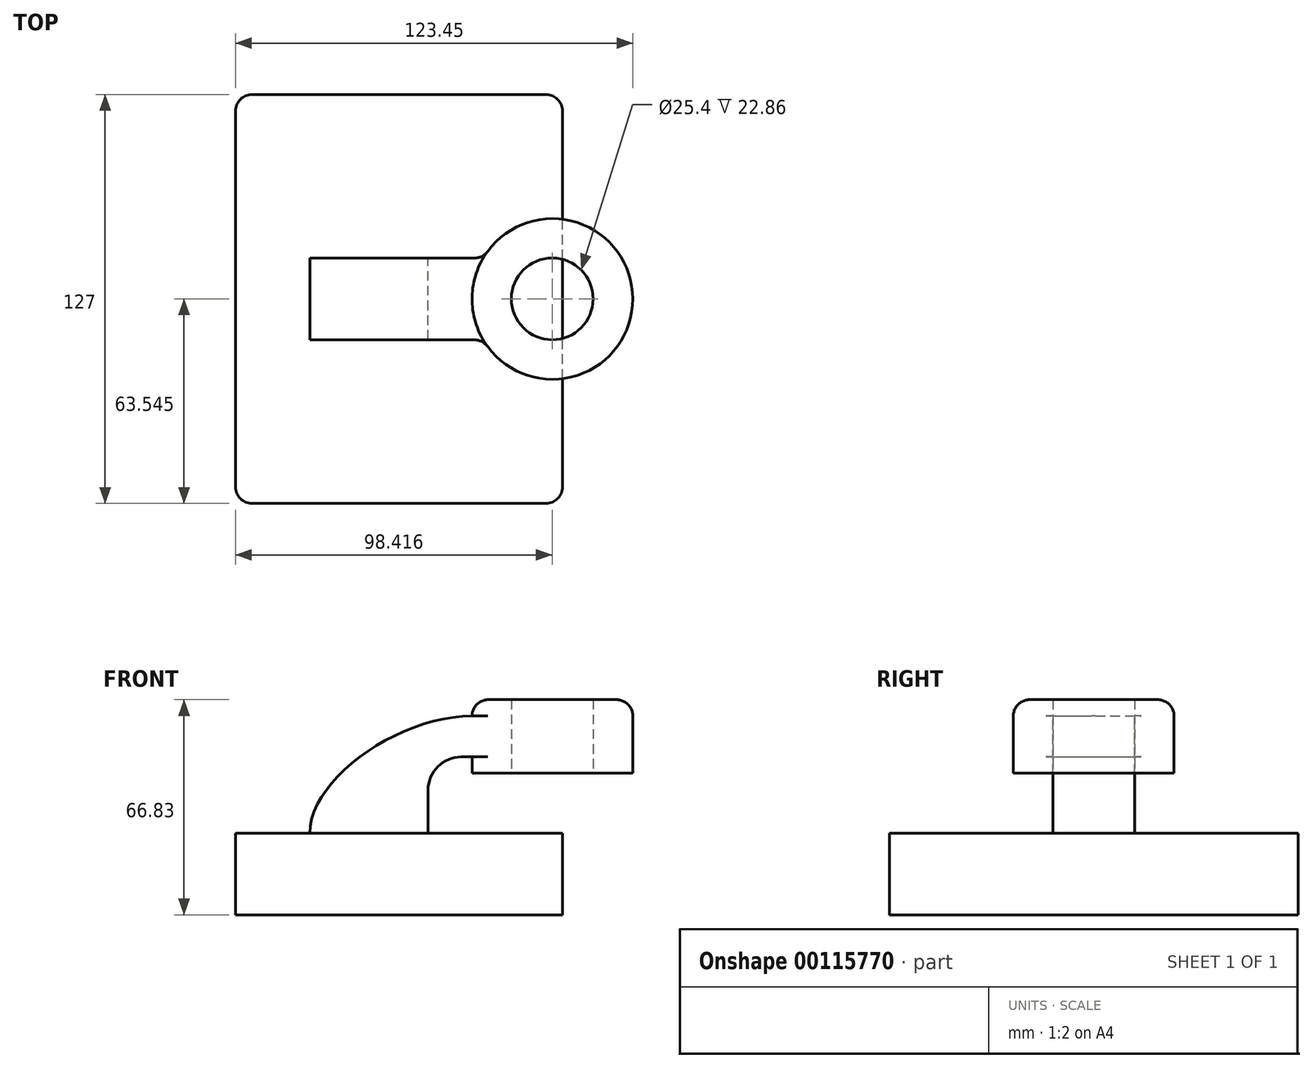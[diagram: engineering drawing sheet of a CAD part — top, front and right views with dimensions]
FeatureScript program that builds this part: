
annotation { "Feature Type Name" : "Feature", "Feature Type Description" : "" }
export const myFeature = defineFeature(function(context is Context, id is Id, definition is map)
    precondition{}
    {
        {
            var Q0;
            Q0=qCreatedBy(makeId("Front.planeOp"),FACE);
            var sketch = newSketch(context, id + "F0", { "sketchPlane" : qUnion([Q0])});
            skLineSegment(sketch, "E0.bottom", {"start": v(-50.8, 12.7) * mm, "end": v(50.8, 12.7) * mm});
            skLineSegment(sketch, "E0.top", {"start": v(-50.8, -12.7) * mm, "end": v(50.8, -12.7) * mm});
            skLineSegment(sketch, "E0.left", {"start": v(-50.8, 12.7) * mm, "end": v(-50.8, -12.7) * mm});
            skLineSegment(sketch, "E0.right", {"start": v(50.8, 12.7) * mm, "end": v(50.8, -12.7) * mm});
            skPoint(sketch, "E0.middle", {"position": v(0, 0) * mm});
            skPoint(sketch, "E1.visualSharp", {"position": v(35.5, 28.49) * mm});
            skLineSegment(sketch, "E2.bottom", {"start": v(22.69, 54.13) * mm, "end": v(72.65, 54.13) * mm});
            skLineSegment(sketch, "E2.top", {"start": v(22.69, 31.27) * mm, "end": v(72.65, 31.27) * mm});
            skLineSegment(sketch, "E2.left", {"start": v(22.69, 54.13) * mm, "end": v(22.69, 31.27) * mm});
            skLineSegment(sketch, "E2.right", {"start": v(72.65, 54.13) * mm, "end": v(72.65, 31.27) * mm});
            skLineSegment(sketch, "E3", {"start": v(47.67, 54.13) * mm, "end": v(47.67, 31.27) * mm});
            skLineSegment(sketch, "E4.0", {"start": v(47.67, 49.05) * mm, "end": v(22.7, 49.05) * mm});
            skLineSegment(sketch, "E5.0", {"start": v(47.67, 36.35) * mm, "end": v(19.36, 36.35) * mm});
            skLineSegment(sketch, "E6", {"start": v(9.02, 12.7) * mm, "end": v(9.02, 26) * mm});
            skFitSpline(sketch, "E7", {"points": [v(-27.74, 12.7) * mm, v(22.7, 49.05) * mm], "startDerivative": vector(0, 50.63) * mm, "endDerivative": vector(68.08, 0) * mm});
            skArc(sketch, "E8", {"start": v(19.36, 36.35) * mm, "mid": v(12.05, 33.32) * mm, "end": v(9.02, 26) * mm});
            skSolve(sketch);
        }
        {
            var Q0;
            Q0=makeQuery(id+"F0.imprint","IMPRINT",FACE,{"disambiguationData":[TD([[makeQuery(id+"F0.imprint","IMPRINT",EDGE,{"derivedFrom":sQuery(id+"F0.wireOp",EDGE,"E0.top")}),1.0]])]});
            extrude(context, id + "F1", {"entities" : qUnion([Q0]), "endBound" : BoundingType.SYMMETRIC, "depth" : 127 * mm});
        }
        {
            var Q0;
            Q0=makeQuery(id+"F0.imprint","IMPRINT",FACE,{"disambiguationData":[TD([[makeQuery(id+"F0.imprint","IMPRINT",EDGE,{"derivedFrom":sQuery(id+"F0.wireOp",EDGE,"E0.top")}),1.0]])]});
            extrude(context, id + "F2", {"entities" : qUnion([Q0]), "operationType" : NewBodyOperationType.ADD, "endBound" : BoundingType.SYMMETRIC, "depth" : 127 * mm});
        }
        {
            var Q0;
            {var subQ0=sQuery(id+"F0.wireOp",EDGE,"E6");Q0=makeQuery(id+"F0.imprint","IMPRINT",FACE,{"disambiguationData":[TD([[makeQuery(id+"F0.imprint","IMPRINT",EDGE,{"derivedFrom":subQ0}),1.0]])]});}
            var Q1;
            {var subQ5=sQuery(id+"F0.wireOp",EDGE,"E4.0");Q1=makeQuery(id+"F0.imprint","IMPRINT",FACE,{"disambiguationData":[TD([[makeQuery(id+"F0.imprint","IMPRINT",EDGE,{"derivedFrom":subQ5}),1.0]])]});}
            extrude(context, id + "F3", {"entities" : qUnion([Q0, Q1]), "operationType" : NewBodyOperationType.ADD, "endBound" : BoundingType.SYMMETRIC, "depth" : 25.4 * mm});
        }
        {
            var Q0;
            {var subQ4=sQuery(id+"F0.wireOp",EDGE,"E2.right");Q0=makeQuery(id+"F0.imprint","IMPRINT",FACE,{"disambiguationData":[TD([[makeQuery(id+"F0.imprint","IMPRINT",EDGE,{"derivedFrom":subQ4}),-1.0]])]});}
            var Q1;
            Q1=sQuery(id+"F0.wireOp",EDGE,"E3");
            revolve(context, id + "F4", {"operationType" : NewBodyOperationType.ADD, "entities" : qUnion([Q0]), "axis" : qUnion([Q1]), "revolveType" : RevolveType.FULL});
        }
        {
            var Q0;
            Q0=makeQuery(id+"F3.opExtrude","CAP_EDGE",EDGE,{"disambiguationData":[OSD([sQuery(id+"F0.wireOp",EDGE,"E0.bottom")])],"isStart":false});
            var Q1;
            Q1=makeQuery(id+"F3.opExtrude","SWEPT_EDGE",EDGE,{"disambiguationData":[OSD([sQuery(id+"F0.wireOp",EDGE,"E0.bottom"),sQuery(id+"F0.wireOp",EDGE,"E6")])]});
            var Q2;
            Q2=makeQuery(id+"F3.opExtrude","SWEPT_EDGE",EDGE,{"disambiguationData":[OSD([sQuery(id+"F0.wireOp",EDGE,"E0.bottom"),sQuery(id+"F0.wireOp",EDGE,"E7")])]});
            var Q3;
            Q3=makeQuery(id+"F3.opExtrude","CAP_EDGE",EDGE,{"disambiguationData":[OSD([sQuery(id+"F0.wireOp",EDGE,"E0.bottom")])],"isStart":true});
            var Q4;
            Q4=makeQuery(id+"F1.opExtrude","CAP_EDGE",EDGE,{"disambiguationData":[OSD([sQuery(id+"F0.wireOp",EDGE,"E0.left")])],"isStart":false});
            var Q5;
            Q5=makeQuery(id+"F1.opExtrude","CAP_EDGE",EDGE,{"disambiguationData":[OSD([sQuery(id+"F0.wireOp",EDGE,"E0.left")])],"isStart":true});
            var Q6;
            Q6=makeQuery(id+"F1.opExtrude","CAP_EDGE",EDGE,{"disambiguationData":[OSD([sQuery(id+"F0.wireOp",EDGE,"E0.right")])],"isStart":false});
            var Q7;
            Q7=makeQuery(id+"F1.opExtrude","CAP_EDGE",EDGE,{"disambiguationData":[OSD([sQuery(id+"F0.wireOp",EDGE,"E0.right")])],"isStart":true});
            fillet(context, id + "F5", {"entities" : qUnion([Q0, Q1, Q2, Q3, Q4, Q5, Q6, Q7]), "radius" : 5.08 * mm, "tangentPropagation" : true, "allowEdgeOverflow" : false});
        }
        {
            var Q0;
            Q0=makeQuery(id+"F4.boolean.opBoolean","INTERSECT",EDGE,{"derivedFrom":[makeQuery(id+"F3.opExtrude","CAP_FACE",FACE,{"disambiguationData":[OSD([sQuery(id+"F0.wireOp",EDGE,"E0.bottom"),sQuery(id+"F0.wireOp",EDGE,"E3"),sQuery(id+"F0.wireOp",EDGE,"E4.0"),sQuery(id+"F0.wireOp",EDGE,"E5.0"),sQuery(id+"F0.wireOp",EDGE,"E6"),sQuery(id+"F0.wireOp",EDGE,"E7"),sQuery(id+"F0.wireOp",EDGE,"E8")])],"isStart":false}),makeQuery(id+"F4.opRevolve","SWEPT_FACE",FACE,{"disambiguationData":[OSD([sQuery(id+"F0.wireOp",EDGE,"E2.right")])]})]});
            var Q1;
            Q1=makeQuery(id+"F4.boolean.opBoolean","INTERSECT",EDGE,{"derivedFrom":[makeQuery(id+"F3.opExtrude","CAP_FACE",FACE,{"disambiguationData":[OSD([sQuery(id+"F0.wireOp",EDGE,"E0.bottom"),sQuery(id+"F0.wireOp",EDGE,"E3"),sQuery(id+"F0.wireOp",EDGE,"E4.0"),sQuery(id+"F0.wireOp",EDGE,"E5.0"),sQuery(id+"F0.wireOp",EDGE,"E6"),sQuery(id+"F0.wireOp",EDGE,"E7"),sQuery(id+"F0.wireOp",EDGE,"E8")])],"isStart":true}),makeQuery(id+"F4.opRevolve","SWEPT_FACE",FACE,{"disambiguationData":[OSD([sQuery(id+"F0.wireOp",EDGE,"E2.right")])]})]});
            fillet(context, id + "F6", {"entities" : qUnion([Q0, Q1]), "radius" : 5.08 * mm, "tangentPropagation" : true, "allowEdgeOverflow" : false});
        }
        {
            var Q0;
            Q0=makeQuery(id+"F4.opRevolve","SWEPT_EDGE",EDGE,{"disambiguationData":[OSD([sQuery(id+"F0.wireOp",EDGE,"E2.bottom"),sQuery(id+"F0.wireOp",EDGE,"E2.right")])]});
            fillet(context, id + "F7", {"entities" : qUnion([Q0]), "radius" : 5.08 * mm, "tangentPropagation" : true, "allowEdgeOverflow" : false});
        }
        {
            var Q0;
            Q0=makeQuery(id+"F4.opRevolve","SWEPT_FACE",FACE,{"disambiguationData":[OSD([sQuery(id+"F0.wireOp",EDGE,"E2.top")])]});
            cPlane(context, id + "F8", {"entities" : qUnion([Q0]), "cplaneType" : CPlaneType.OFFSET, "offset" : 0 * mm, "width" : 152.4 * mm, "height" : 152.4 * mm});
        }
        {
            var Q0;
            Q0=qCreatedBy(id+"F8.planeOp",FACE);
            var sketch = newSketch(context, id + "F9", { "sketchPlane" : qUnion([Q0])});
            skLineSegment(sketch, "E9", {"start": v(47.62, -0.05) * mm, "end": v(72.46, -0.05) * mm});
            skSolve(sketch);
        }
        {
            var Q0;
            Q0=sQuery(id+"F9.wireOp",VERTEX,"E9.start");
            var Q1;
            Q1=makeQuery(id+"F1.opExtrude","SWEPT_BODY",BODY,{"disambiguationData":[OSD([sQuery(id+"F0.wireOp",EDGE,"E0.bottom"),sQuery(id+"F0.wireOp",EDGE,"E0.top"),sQuery(id+"F0.wireOp",EDGE,"E0.left"),sQuery(id+"F0.wireOp",EDGE,"E0.right")])]});
            hole(context, id + "F10", {"style" : HoleStyle.SIMPLE, "endStyle" : HoleEndStyle.THROUGH, "holeDiameter" : 25.4 * mm, "startFromSketch" : true, "locations" : qUnion([Q0]), "scope" : qUnion([Q1]), "isTappedThrough" : true});
        }
    });
